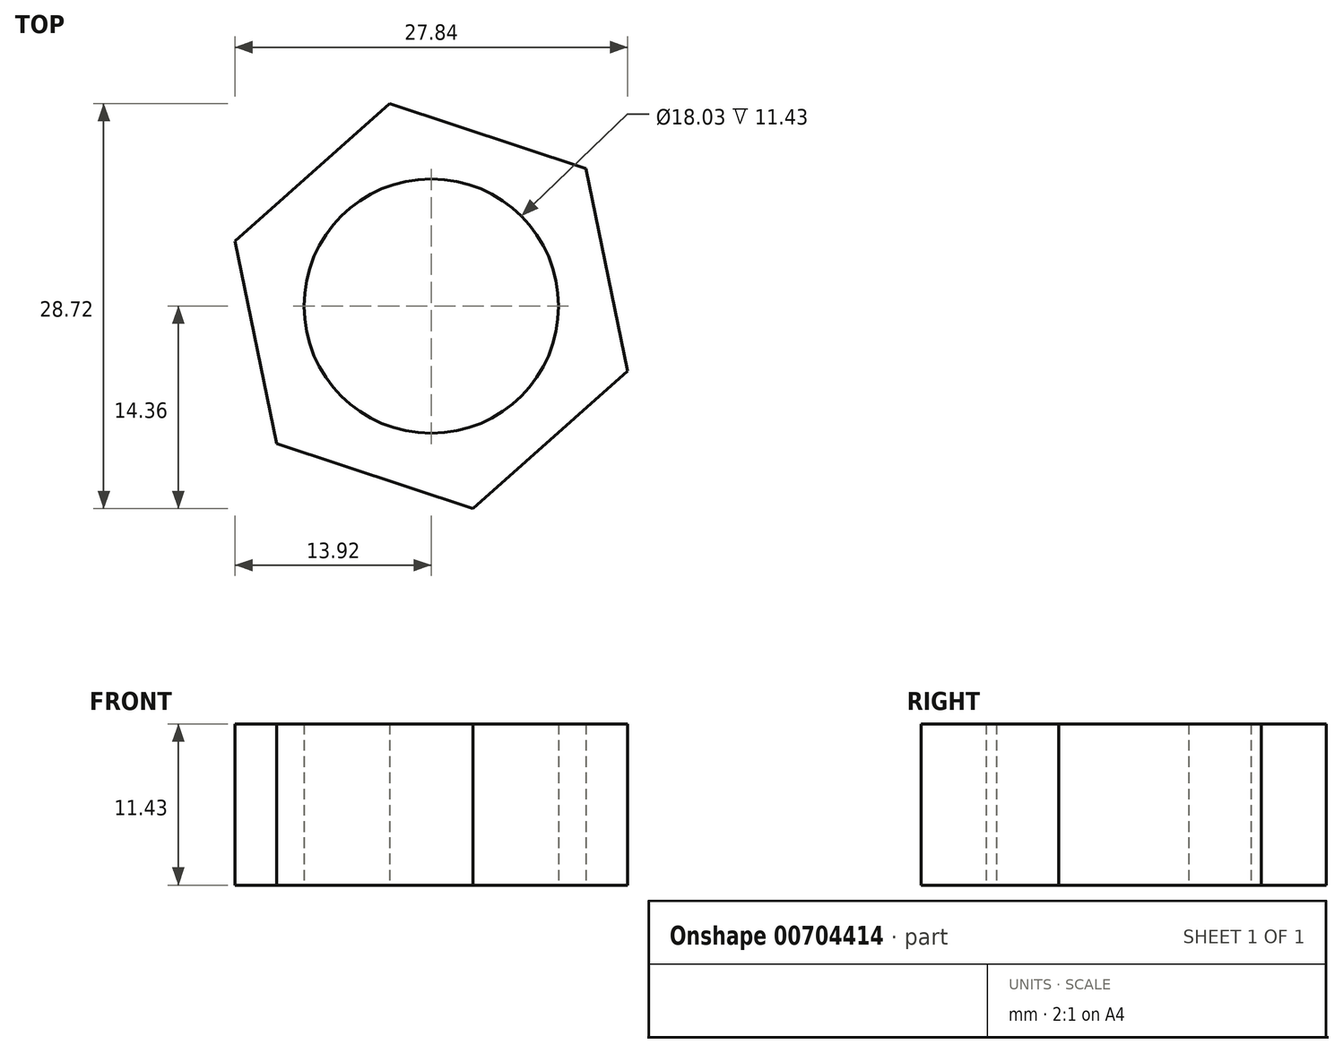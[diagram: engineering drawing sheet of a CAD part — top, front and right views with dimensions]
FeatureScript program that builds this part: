
annotation { "Feature Type Name" : "Feature", "Feature Type Description" : "" }
export const myFeature = defineFeature(function(context is Context, id is Id, definition is map)
    precondition{}
    {
        {
            var Q0;
            Q0=qCreatedBy(makeId("Top.planeOp"),FACE);
            var sketch = newSketch(context, id + "F0", { "sketchPlane" : qUnion([Q0])});
            skCircle(sketch, "E0", {"center": v(0, 0) * mm, "radius": 9.02 * mm});
            skCircle(sketch, "E1.cCircle", {"center": v(0, 0) * mm, "radius": 12.7 * mm, "construction": true});
            skLineSegment(sketch, "E1.0", {"start": v(13.92, -4.61) * mm, "end": v(2.96, -14.36) * mm});
            skLineSegment(sketch, "E1.1", {"start": v(2.96, -14.36) * mm, "end": v(-10.96, -9.75) * mm});
            skLineSegment(sketch, "E1.2", {"start": v(-10.96, -9.75) * mm, "end": v(-13.92, 4.61) * mm});
            skLineSegment(sketch, "E1.3", {"start": v(-13.92, 4.61) * mm, "end": v(-2.96, 14.36) * mm});
            skLineSegment(sketch, "E1.4", {"start": v(-2.96, 14.36) * mm, "end": v(10.96, 9.75) * mm});
            skLineSegment(sketch, "E1.5", {"start": v(10.96, 9.75) * mm, "end": v(13.92, -4.61) * mm});
            skPoint(sketch, "E1.0.midPoint", {"position": v(8.44, -9.49) * mm});
            skSolve(sketch);
        }
        {
            var Q0;
            Q0 = qSketchRegion(id + "F0", true);
            extrude(context, id + "F1", {"entities" : qUnion([Q0]), "depth" : 11.43 * mm, "offsetDistance" : 25.4 * mm});
        }
    });
